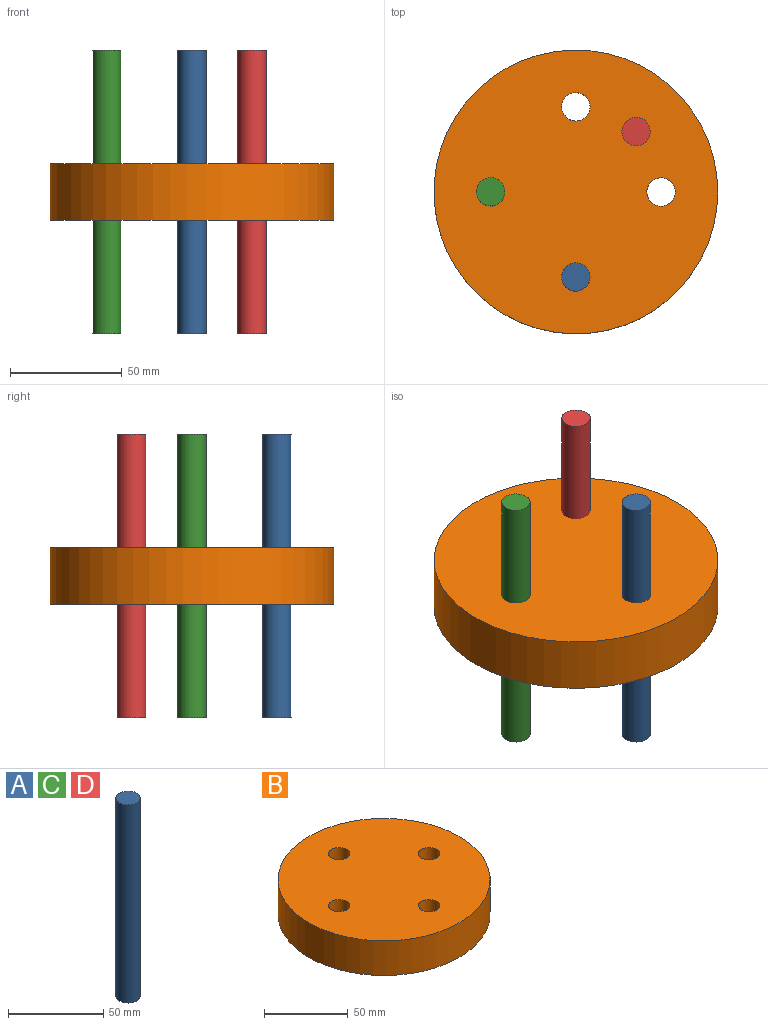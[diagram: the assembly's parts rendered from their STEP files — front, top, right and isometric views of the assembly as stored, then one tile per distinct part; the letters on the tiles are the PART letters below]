
ASSEMBLY  parts=4 mates=1
PART A: 3 faces, bbox 12.7x12.7x127 mm
  f0: cylinder r=6.35mm len=127mm, axis (0,0,-1), area 5067.1mm2, adj f1,f2
  f1: plane 12.7x12.7mm, normal (0,0,1), area 126.7mm2, adj f0
  f2: plane 12.7x12.7mm, normal (0,0,-1), area 126.7mm2, adj f0
PART B: 7 faces, bbox 127x127x25.4 mm
  f0: cylinder r=63.5mm len=127mm, axis (0,0,-1), area 10134.1mm2, adj f1,f2
  f1: plane 127x127mm, normal (0,0,1), area 12161mm2, adj f0,f3,f4,f5,f6
  f2: plane 127x127mm, normal (0,0,-1), area 12161mm2, adj f0,f3,f4,f5,f6
  f3: cylinder r=6.35mm len=25.4mm, axis (0,0,1), area 1013.4mm2, adj f1,f2
  f4: cylinder r=6.35mm len=25.4mm, axis (0,0,1), area 1013.4mm2, adj f1,f2
  f5: cylinder r=6.35mm len=25.4mm, axis (0,0,1), area 1013.4mm2, adj f1,f2
  f6: cylinder r=6.35mm len=25.4mm, axis (0,0,1), area 1013.4mm2, adj f1,f2
PART C: same geometry as A
PART D: same geometry as A
PLACE A rot(axis=(0,0,1),90deg) t=(0,-38.1,-12.7)mm
PLACE B t=(0,0,-25.4)mm
PLACE C t=(-38.1,0,-12.7)mm
PLACE D rot(axis=(0,0,-1),135deg) t=(26.94,26.94,-12.7)mm
MATE fastened C.f0 <-> B.f6  axis (0,0,1) through (-38.1,0,50.8)mm
